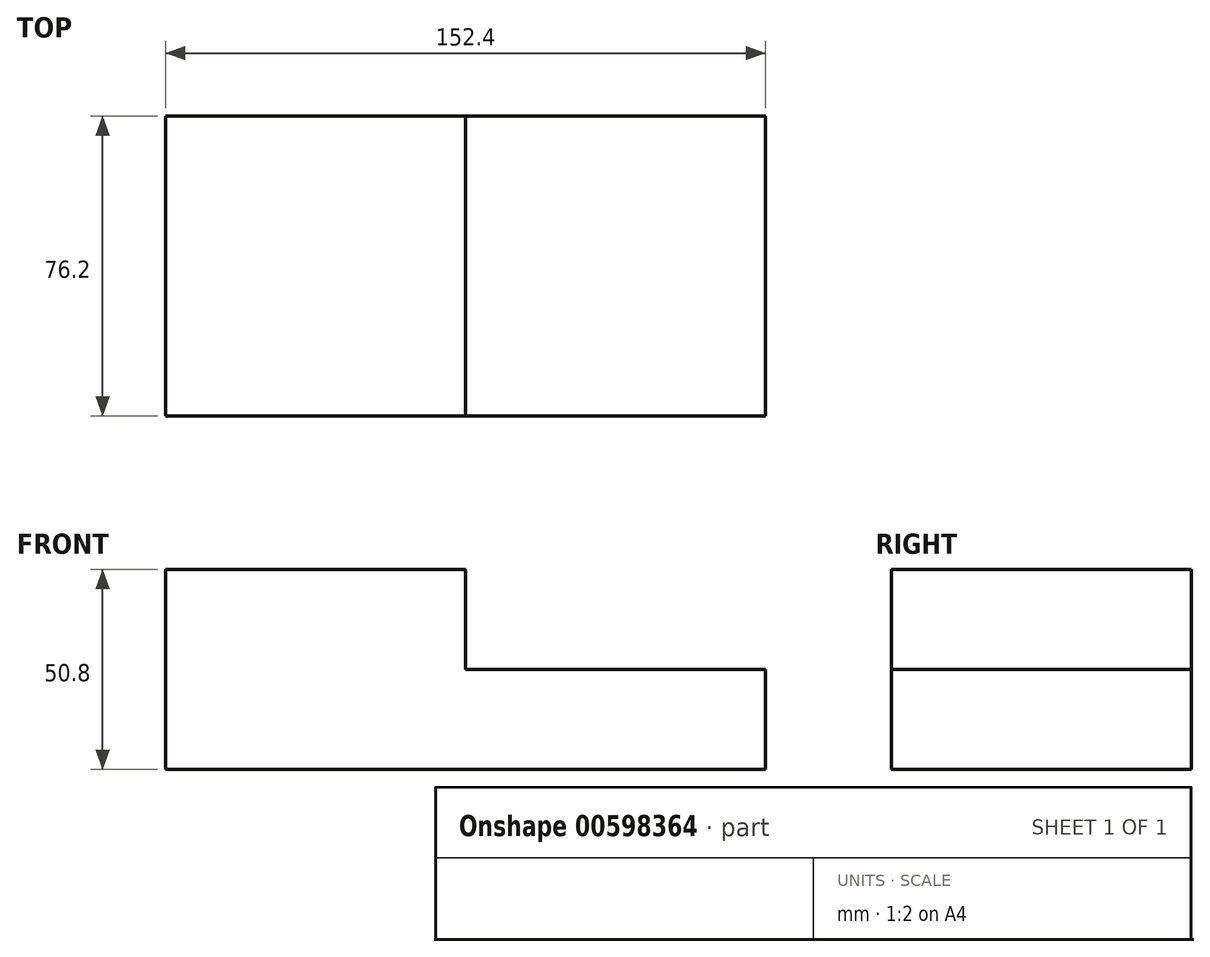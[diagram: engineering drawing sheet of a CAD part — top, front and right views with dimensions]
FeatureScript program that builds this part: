
annotation { "Feature Type Name" : "Feature", "Feature Type Description" : "" }
export const myFeature = defineFeature(function(context is Context, id is Id, definition is map)
    precondition{}
    {
        {
            var Q0;
            Q0=qCreatedBy(makeId("Front.planeOp"),FACE);
            var sketch = newSketch(context, id + "F0", { "sketchPlane" : qUnion([Q0])});
            skLineSegment(sketch, "E0", {"start": v(0, 0) * mm, "end": v(0, 50.8) * mm});
            skLineSegment(sketch, "E1", {"start": v(0, 50.8) * mm, "end": v(76.2, 50.8) * mm});
            skLineSegment(sketch, "E2", {"start": v(0, 0) * mm, "end": v(152.4, 0) * mm});
            skLineSegment(sketch, "E3", {"start": v(76.2, 50.8) * mm, "end": v(76.2, 25.4) * mm});
            skLineSegment(sketch, "E4", {"start": v(76.2, 25.4) * mm, "end": v(152.4, 25.4) * mm});
            skLineSegment(sketch, "E5", {"start": v(152.4, 0) * mm, "end": v(152.4, 25.4) * mm});
            skSolve(sketch);
        }
        {
            var Q0;
            Q0 = qSketchRegion(id + "F0", true);
            extrude(context, id + "F1", {"entities" : qUnion([Q0]), "depth" : 76.2 * mm, "offsetDistance" : 25.4 * mm});
        }
    });
